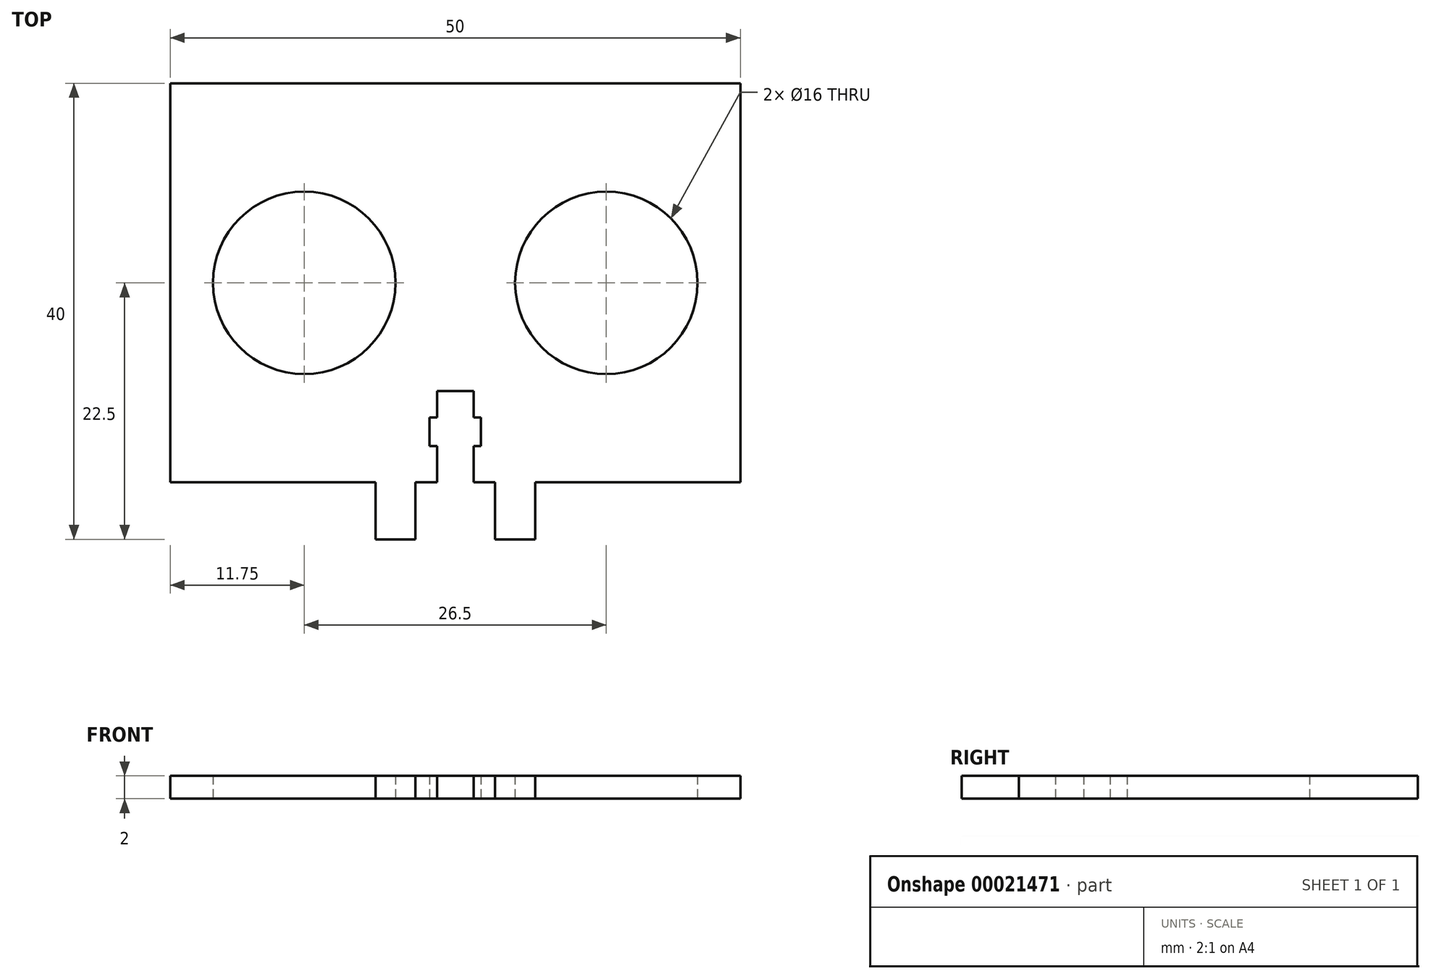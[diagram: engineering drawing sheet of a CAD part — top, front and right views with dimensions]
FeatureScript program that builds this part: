
annotation { "Feature Type Name" : "Feature", "Feature Type Description" : "" }
export const myFeature = defineFeature(function(context is Context, id is Id, definition is map)
    precondition{}
    {
        {
            var Q0;
            Q0=qCreatedBy(makeId("Top.planeOp"),FACE);
            var sketch = newSketch(context, id + "F0", { "sketchPlane" : qUnion([Q0])});
            skLineSegment(sketch, "E0.rect.bottom", {"start": v(25, -17.5) * mm, "end": v(1.6, -17.5) * mm});
            skLineSegment(sketch, "E0.rect.top", {"start": v(25, 17.5) * mm, "end": v(-25, 17.5) * mm});
            skLineSegment(sketch, "E0.rect.left", {"start": v(25, -17.5) * mm, "end": v(25, 17.5) * mm});
            skLineSegment(sketch, "E0.rect.right", {"start": v(-25, -17.5) * mm, "end": v(-25, 17.5) * mm});
            skPoint(sketch, "E0.rect.middle", {"position": v(0, 0) * mm});
            skLineSegment(sketch, "E1", {"start": v(-29.94, 0) * mm, "end": v(40.04, 0) * mm, "construction": true});
            skCircle(sketch, "E2", {"center": v(-13.25, 0) * mm, "radius": 8 * mm});
            skLineSegment(sketch, "E3", {"start": v(0, 12.7) * mm, "end": v(0, -27.18) * mm, "construction": true});
            skCircle(sketch, "E4.0.MirrorC", {"center": v(13.25, 0) * mm, "radius": 8 * mm});
            skLineSegment(sketch, "E5", {"start": v(-7, -17.5) * mm, "end": v(-7, -22.5) * mm});
            skLineSegment(sketch, "E6", {"start": v(-7, -22.5) * mm, "end": v(-3.5, -22.5) * mm});
            skLineSegment(sketch, "E7", {"start": v(-3.5, -22.5) * mm, "end": v(-3.5, -17.5) * mm});
            skLineSegment(sketch, "E8", {"start": v(-3.5, -17.5) * mm, "end": v(-1.6, -17.5) * mm});
            skLineSegment(sketch, "E9", {"start": v(-1.6, -17.5) * mm, "end": v(-1.6, -14.3) * mm});
            skLineSegment(sketch, "E10", {"start": v(-1.6, -14.3) * mm, "end": v(-2.25, -14.3) * mm});
            skLineSegment(sketch, "E11", {"start": v(-2.25, -14.3) * mm, "end": v(-2.25, -11.8) * mm});
            skLineSegment(sketch, "E12", {"start": v(-2.25, -11.8) * mm, "end": v(-1.6, -11.8) * mm});
            skLineSegment(sketch, "E13", {"start": v(-1.6, -11.8) * mm, "end": v(-1.6, -9.5) * mm});
            skLineSegment(sketch, "E14", {"start": v(-1.6, -9.5) * mm, "end": v(0, -9.5) * mm});
            skLineSegment(sketch, "E15.0.MirrorCS", {"start": v(2.25, -11.8) * mm, "end": v(1.6, -11.8) * mm});
            skLineSegment(sketch, "E15.1.MirrorCS", {"start": v(1.6, -14.3) * mm, "end": v(2.25, -14.3) * mm});
            skLineSegment(sketch, "E15.2.MirrorCS", {"start": v(7, -17.5) * mm, "end": v(7, -22.5) * mm});
            skLineSegment(sketch, "E15.3.MirrorCS", {"start": v(3.5, -22.5) * mm, "end": v(3.5, -17.5) * mm});
            skLineSegment(sketch, "E15.4.MirrorCS", {"start": v(7, -22.5) * mm, "end": v(3.5, -22.5) * mm});
            skLineSegment(sketch, "E15.5.MirrorCS", {"start": v(1.6, -17.5) * mm, "end": v(1.6, -14.3) * mm});
            skLineSegment(sketch, "E15.6.MirrorCS", {"start": v(1.6, -9.5) * mm, "end": v(0, -9.5) * mm});
            skLineSegment(sketch, "E15.7.MirrorCS", {"start": v(3.5, -17.5) * mm, "end": v(1.6, -17.5) * mm});
            skLineSegment(sketch, "E15.8.MirrorCS", {"start": v(1.6, -11.8) * mm, "end": v(1.6, -9.5) * mm});
            skLineSegment(sketch, "E15.9.MirrorCS", {"start": v(2.25, -14.3) * mm, "end": v(2.25, -11.8) * mm});
            skLineSegment(sketch, "E16.trimOffspring", {"start": v(-1.6, -17.5) * mm, "end": v(-25, -17.5) * mm});
            skSolve(sketch);
        }
        {
            var Q0;
            Q0=qSketchRegion(id+"F0",true);
            extrude(context, id + "F1", {"entities" : qUnion([Q0]), "depth" : 2 * mm});
        }
    });
